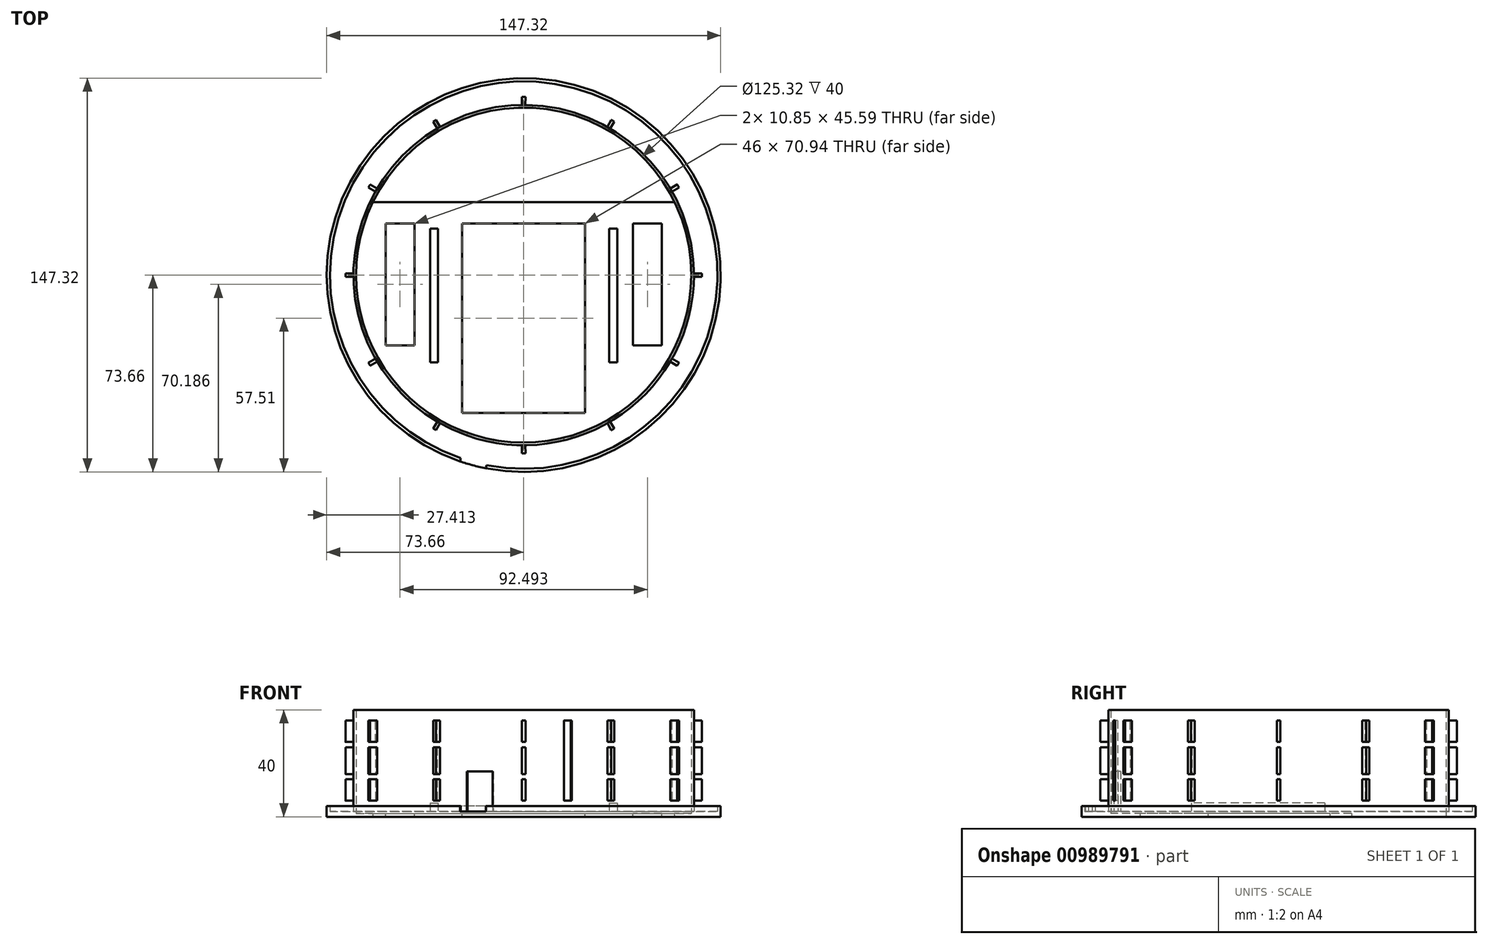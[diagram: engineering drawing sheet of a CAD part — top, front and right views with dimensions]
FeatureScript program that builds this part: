
annotation { "Feature Type Name" : "Feature", "Feature Type Description" : "" }
export const myFeature = defineFeature(function(context is Context, id is Id, definition is map)
    precondition{}
    {
        {
            var Q0;
            Q0=qCreatedBy(makeId("Top.planeOp"),FACE);
            var sketch = newSketch(context, id + "F0", { "sketchPlane" : qUnion([Q0])});
            skCircle(sketch, "E0", {"center": v(0, 0) * mm, "radius": 63.66 * mm, "construction": true});
            skCircle(sketch, "E1", {"center": v(0, 0) * mm, "radius": 73.66 * mm});
            skCircle(sketch, "E2", {"center": v(0, 0) * mm, "radius": 62.66 * mm});
            skPoint(sketch, "E3", {"position": v(0, -63.66) * mm});
            skSolve(sketch);
        }
        {
            var Q0;
            Q0=makeQuery(id+"F0.imprint","IMPRINT",FACE,{"disambiguationData":[TD([[makeQuery(id+"F0.imprint","IMPRINT",EDGE,{"derivedFrom":sQuery(id+"F0.wireOp",EDGE,"E1")}),1.0]])]});
            extrude(context, id + "F1", {"entities" : qUnion([Q0]), "depth" : 2 * mm, "offsetDistance" : 25 * mm});
        }
        {
            var Q0;
            Q0=makeQuery(id+"F1.opExtrude","CAP_FACE",FACE,{"disambiguationData":[OSD([sQuery(id+"F0.wireOp",EDGE,"E1"),sQuery(id+"F0.wireOp",EDGE,"E2")])],"isStart":false});
            var sketch = newSketch(context, id + "F2", { "sketchPlane" : qUnion([Q0])});
            skCircle(sketch, "E4.0", {"center": v(0, 0) * mm, "radius": 63.66 * mm});
            skCircle(sketch, "E5.0", {"center": v(0, 0) * mm, "radius": 62.66 * mm});
            skSolve(sketch);
        }
        {
            var Q0;
            Q0 = qSketchRegion(id + "F2", true);
            extrude(context, id + "F3", {"entities" : qUnion([Q0]), "operationType" : NewBodyOperationType.ADD, "depth" : 38 * mm, "offsetDistance" : 25 * mm});
        }
        {
            var Q0;
            Q0=makeQuery(id+"F1.opExtrude","CAP_FACE",FACE,{"disambiguationData":[OSD([sQuery(id+"F0.wireOp",EDGE,"E1"),sQuery(id+"F0.wireOp",EDGE,"E2")])],"isStart":false});
            var sketch = newSketch(context, id + "F4", { "sketchPlane" : qUnion([Q0])});
            skCircle(sketch, "E6.0", {"center": v(0, 0) * mm, "radius": 73.66 * mm});
            skCircle(sketch, "E7", {"center": v(0, 0) * mm, "radius": 72.46 * mm});
            skPoint(sketch, "E8", {"position": v(0, 72.46) * mm});
            skPoint(sketch, "E9", {"position": v(0, 73.66) * mm});
            skSolve(sketch);
        }
        {
            var Q0;
            Q0 = qSketchRegion(id + "F4", true);
            extrude(context, id + "F5", {"entities" : qUnion([Q0]), "operationType" : NewBodyOperationType.ADD, "depth" : 2 * mm, "offsetDistance" : 25 * mm});
        }
        {
            var Q0;
            Q0=qCreatedBy(makeId("Top.planeOp"),FACE);
            var sketch = newSketch(context, id + "F6", { "sketchPlane" : qUnion([Q0])});
            skLineSegment(sketch, "E10", {"start": v(0, 0) * mm, "end": v(0, -63.75) * mm, "construction": true});
            skSolve(sketch);
        }
        {
            var Q0;
            Q0=qCreatedBy(makeId("Front.planeOp"),FACE);
            var sketch = newSketch(context, id + "F7", { "sketchPlane" : qUnion([Q0])});
            skLineSegment(sketch, "E11", {"start": v(63.66, 40) * mm, "end": v(63.66, 2) * mm, "construction": true});
            skLineSegment(sketch, "E12", {"start": v(-63.66, 2) * mm, "end": v(-63.66, 40) * mm, "construction": true});
            skPoint(sketch, "E13", {"position": v(-63.66, 21) * mm});
            skLineSegment(sketch, "E14.bottom", {"start": v(-63.66, 26) * mm, "end": v(-66.66, 26) * mm});
            skLineSegment(sketch, "E14.top", {"start": v(-63.66, 16) * mm, "end": v(-66.66, 16) * mm});
            skLineSegment(sketch, "E14.left", {"start": v(-63.66, 26) * mm, "end": v(-63.66, 16) * mm});
            skLineSegment(sketch, "E14.right", {"start": v(-66.66, 26) * mm, "end": v(-66.66, 16) * mm});
            skLineSegment(sketch, "E15.bottom", {"start": v(-63.66, 28) * mm, "end": v(-66.66, 28) * mm});
            skLineSegment(sketch, "E15.top", {"start": v(-63.66, 36) * mm, "end": v(-66.66, 36) * mm});
            skLineSegment(sketch, "E15.left", {"start": v(-63.66, 28) * mm, "end": v(-63.66, 36) * mm});
            skLineSegment(sketch, "E15.right", {"start": v(-66.66, 28) * mm, "end": v(-66.66, 36) * mm});
            skLineSegment(sketch, "E16.bottom", {"start": v(-63.66, 14) * mm, "end": v(-66.66, 14) * mm});
            skLineSegment(sketch, "E16.top", {"start": v(-63.66, 6) * mm, "end": v(-66.66, 6) * mm});
            skLineSegment(sketch, "E16.left", {"start": v(-63.66, 14) * mm, "end": v(-63.66, 6) * mm});
            skLineSegment(sketch, "E16.right", {"start": v(-66.66, 14) * mm, "end": v(-66.66, 6) * mm});
            skSolve(sketch);
        }
        {
            var Q0;
            Q0=qCreatedBy(makeId("Front.planeOp"),FACE);
            var sketch = newSketch(context, id + "F8", { "sketchPlane" : qUnion([Q0])});
            skLineSegment(sketch, "E17", {"start": v(0, 0) * mm, "end": v(0, 90.7) * mm, "construction": true});
            skSolve(sketch);
        }
        {
            var Q0;
            Q0 = qSketchRegion(id + "F7", true);
            var Q1;
            Q1=sQuery(id+"F8.wireOp",EDGE,"E17");
            revolve(context, id + "F9", {"surfaceOperationType" : NewSurfaceOperationType.NEW, "entities" : qUnion([Q0]), "axis" : qUnion([Q1]), "revolveType" : RevolveType.SYMMETRIC, "angle" : 1.12 * degree});
        }
        {
            var Q0;
            Q0=makeQuery(id+"F9.opRevolve","SWEPT_BODY",BODY,{"disambiguationData":[OSD([sQuery(id+"F7.wireOp",EDGE,"E15.bottom"),sQuery(id+"F7.wireOp",EDGE,"E15.top"),sQuery(id+"F7.wireOp",EDGE,"E15.left"),sQuery(id+"F7.wireOp",EDGE,"E15.right")])]});
            var Q1;
            Q1=makeQuery(id+"F9.opRevolve","SWEPT_BODY",BODY,{"disambiguationData":[OSD([sQuery(id+"F7.wireOp",EDGE,"E14.bottom"),sQuery(id+"F7.wireOp",EDGE,"E14.top"),sQuery(id+"F7.wireOp",EDGE,"E14.left"),sQuery(id+"F7.wireOp",EDGE,"E14.right")])]});
            var Q2;
            Q2=makeQuery(id+"F9.opRevolve","SWEPT_BODY",BODY,{"disambiguationData":[OSD([sQuery(id+"F7.wireOp",EDGE,"E16.bottom"),sQuery(id+"F7.wireOp",EDGE,"E16.top"),sQuery(id+"F7.wireOp",EDGE,"E16.left"),sQuery(id+"F7.wireOp",EDGE,"E16.right")])]});
            var Q3;
            Q3=sQuery(id+"F8.wireOp",EDGE,"E17");
            circularPattern(context, id + "F10", {"entities" : qUnion([Q0, Q1, Q2]), "axis" : qUnion([Q3]), "angle" : 360 * degree, "instanceCount" : 12, "equalSpace" : true});
        }
        {
            var Q0;
            Q0=qCreatedBy(makeId("Top.planeOp"),FACE);
            var sketch = newSketch(context, id + "F11", { "sketchPlane" : qUnion([Q0])});
            skPoint(sketch, "E18.0", {"position": v(31.83, -55.13) * mm});
            skLineSegment(sketch, "E19", {"start": v(0, 0) * mm, "end": v(31.83, -55.13) * mm, "construction": true});
            skCircle(sketch, "E20.0", {"center": v(0, 0) * mm, "radius": 62.66 * mm, "construction": true});
            skPoint(sketch, "E21", {"position": v(0, -62.66) * mm});
            skPoint(sketch, "E22", {"position": v(31.33, -54.27) * mm});
            skLineSegment(sketch, "E23", {"start": v(0, -62.66) * mm, "end": v(31.33, -54.27) * mm, "construction": true});
            skPoint(sketch, "E24", {"position": v(15.67, -58.46) * mm});
            skLineSegment(sketch, "E25", {"start": v(15.67, -58.46) * mm, "end": v(0, 0) * mm, "construction": true});
            skLineSegment(sketch, "E26.MirrorCS", {"start": v(-15.67, -58.46) * mm, "end": v(0, 0) * mm, "construction": true});
            skCircle(sketch, "E27.0", {"center": v(0, 0) * mm, "radius": 63.66 * mm, "construction": true});
            skLineSegment(sketch, "E28", {"start": v(15.67, -58.46) * mm, "end": v(16.48, -61.5) * mm, "construction": true});
            skLineSegment(sketch, "E29", {"start": v(-15.67, -58.46) * mm, "end": v(-16.48, -61.5) * mm, "construction": true});
            skSolve(sketch);
        }
        {
            var Q0;
            Q0=sQuery(id+"F11.wireOp",VERTEX,"E28.end");
            var Q1;
            Q1=sQuery(id+"F11.wireOp",EDGE,"E25");
            cPlane(context, id + "F12", {"entities" : qUnion([Q0, Q1]), "cplaneType" : CPlaneType.LINE_POINT, "offset" : 25 * mm, "width" : 150 * mm, "height" : 150 * mm});
        }
        {
            var Q0;
            Q0=qCreatedBy(id+"F12.planeOp",FACE);
            var sketch = newSketch(context, id + "F13", { "sketchPlane" : qUnion([Q0])});
            skLineSegment(sketch, "E30.0", {"start": v(61.5, 2) * mm, "end": v(61.5, 40) * mm, "construction": true});
            skLineSegment(sketch, "E30.1", {"start": v(-61.5, 40) * mm, "end": v(-61.5, 2) * mm, "construction": true});
            skLineSegment(sketch, "E31", {"start": v(61.5, 40) * mm, "end": v(-61.5, 40) * mm, "construction": true});
            skLineSegment(sketch, "E32", {"start": v(61.5, 2) * mm, "end": v(-61.5, 2) * mm});
            skLineSegment(sketch, "E33.bottom", {"start": v(1.5, 36) * mm, "end": v(-1.5, 36) * mm});
            skLineSegment(sketch, "E33.top", {"start": v(1.5, 6) * mm, "end": v(-1.5, 6) * mm});
            skLineSegment(sketch, "E33.left", {"start": v(1.5, 36) * mm, "end": v(1.5, 6) * mm});
            skLineSegment(sketch, "E33.right", {"start": v(-1.5, 36) * mm, "end": v(-1.5, 6) * mm});
            skLineSegment(sketch, "E34", {"start": v(61.5, 21) * mm, "end": v(-61.5, 21) * mm, "construction": true});
            skPoint(sketch, "E35.0", {"position": v(61.5, 36) * mm});
            skPoint(sketch, "E35.1", {"position": v(61.5, 6) * mm});
            skLineSegment(sketch, "E36", {"start": v(61.5, 36) * mm, "end": v(-61.5, 36) * mm, "construction": true});
            skLineSegment(sketch, "E37", {"start": v(61.5, 6) * mm, "end": v(-61.5, 6) * mm, "construction": true});
            skSolve(sketch);
        }
        {
            var Q0;
            Q0 = qSketchRegion(id + "F13", true);
            extrude(context, id + "F14", {"entities" : qUnion([Q0]), "operationType" : NewBodyOperationType.REMOVE, "endBound" : BoundingType.UP_TO_NEXT, "depth" : 25 * mm, "offsetDistance" : 25 * mm});
        }
        {
            var Q0;
            Q0=sQuery(id+"F11.wireOp",VERTEX,"E29.end");
            var Q1;
            Q1=sQuery(id+"F11.wireOp",EDGE,"E26.MirrorCS");
            cPlane(context, id + "F15", {"entities" : qUnion([Q0, Q1]), "cplaneType" : CPlaneType.LINE_POINT, "offset" : 25 * mm, "width" : 150 * mm, "height" : 150 * mm});
        }
        {
            var Q0;
            Q0=qCreatedBy(id+"F15.planeOp",FACE);
            var sketch = newSketch(context, id + "F16", { "sketchPlane" : qUnion([Q0])});
            skLineSegment(sketch, "E38.0", {"start": v(61.5, 2) * mm, "end": v(61.5, 40) * mm, "construction": true});
            skLineSegment(sketch, "E38.1", {"start": v(-61.5, 40) * mm, "end": v(-61.5, 2) * mm, "construction": true});
            skLineSegment(sketch, "E39", {"start": v(61.5, 40) * mm, "end": v(-61.5, 40) * mm, "construction": true});
            skLineSegment(sketch, "E40", {"start": v(-61.5, 2) * mm, "end": v(61.5, 2) * mm, "construction": true});
            skLineSegment(sketch, "E41.bottom", {"start": v(-5, 17) * mm, "end": v(5, 17) * mm});
            skLineSegment(sketch, "E41.top", {"start": v(-5, 2) * mm, "end": v(5, 2) * mm});
            skLineSegment(sketch, "E41.left", {"start": v(-5, 17) * mm, "end": v(-5, 2) * mm});
            skLineSegment(sketch, "E41.right", {"start": v(5, 17) * mm, "end": v(5, 2) * mm});
            skSolve(sketch);
        }
        {
            var Q0;
            Q0 = qSketchRegion(id + "F16", true);
            extrude(context, id + "F17", {"entities" : qUnion([Q0]), "operationType" : NewBodyOperationType.REMOVE, "endBound" : BoundingType.SYMMETRIC, "depth" : 25 * mm, "offsetDistance" : 25 * mm});
        }
        {
            var Q0;
            Q0=qCreatedBy(makeId("Top.planeOp"),FACE);
            var sketch = newSketch(context, id + "F18", { "sketchPlane" : qUnion([Q0])});
            skCircle(sketch, "E42.0", {"center": v(0, 0) * mm, "radius": 62.66 * mm, "construction": true});
            skLineSegment(sketch, "E43", {"start": v(-56.38, 27.34) * mm, "end": v(56.38, 27.34) * mm});
            skPoint(sketch, "E44", {"position": v(0, 27.34) * mm});
            skPoint(sketch, "E45", {"position": v(0, -62.66) * mm});
            skArc(sketch, "E46", {"start": v(-56.38, 27.34) * mm, "mid": v(0, -62.66) * mm, "end": v(56.38, 27.34) * mm});
            skSolve(sketch);
        }
        {
            var Q0;
            Q0 = qSketchRegion(id + "F18", true);
            extrude(context, id + "F19", {"entities" : qUnion([Q0]), "operationType" : NewBodyOperationType.ADD, "depth" : 1.2 * mm, "offsetDistance" : 25 * mm});
        }
        {
            var Q0;
            Q0=makeQuery(id+"F19.opExtrude","CAP_FACE",FACE,{"disambiguationData":[OSD([sQuery(id+"F18.wireOp",EDGE,"E43"),sQuery(id+"F18.wireOp",EDGE,"E46")])],"isStart":false});
            var sketch = newSketch(context, id + "F20", { "sketchPlane" : qUnion([Q0])});
            skLineSegment(sketch, "E47.bottom", {"start": v(-35, 17.34) * mm, "end": v(-32, 17.34) * mm});
            skLineSegment(sketch, "E47.top", {"start": v(-35, -32.66) * mm, "end": v(-32, -32.66) * mm});
            skLineSegment(sketch, "E47.left", {"start": v(-35, 17.34) * mm, "end": v(-35, -32.66) * mm});
            skLineSegment(sketch, "E47.right", {"start": v(-32, 17.34) * mm, "end": v(-32, -32.66) * mm});
            skLineSegment(sketch, "E48.bottom", {"start": v(32, 17.34) * mm, "end": v(35, 17.34) * mm});
            skLineSegment(sketch, "E48.top", {"start": v(32, -32.66) * mm, "end": v(35, -32.66) * mm});
            skLineSegment(sketch, "E48.left", {"start": v(32, 17.34) * mm, "end": v(32, -32.66) * mm});
            skLineSegment(sketch, "E48.right", {"start": v(35, 17.34) * mm, "end": v(35, -32.66) * mm});
            skLineSegment(sketch, "E49", {"start": v(-32, 17.34) * mm, "end": v(32, 17.34) * mm, "construction": true});
            skPoint(sketch, "E50", {"position": v(0, 17.34) * mm});
            skSolve(sketch);
        }
        {
            var Q0;
            Q0 = qSketchRegion(id + "F20", true);
            extrude(context, id + "F21", {"entities" : qUnion([Q0]), "operationType" : NewBodyOperationType.ADD, "depth" : 4 * mm, "offsetDistance" : 25 * mm});
        }
        {
            var Q0;
            Q0=makeQuery(id+"F19.opExtrude","CAP_FACE",FACE,{"disambiguationData":[OSD([sQuery(id+"F18.wireOp",EDGE,"E43"),sQuery(id+"F18.wireOp",EDGE,"E46")])],"isStart":false});
            var sketch = newSketch(context, id + "F22", { "sketchPlane" : qUnion([Q0])});
            skLineSegment(sketch, "E51.bottom", {"start": v(-23, 19.32) * mm, "end": v(23, 19.32) * mm});
            skLineSegment(sketch, "E51.top", {"start": v(-23, -51.62) * mm, "end": v(23, -51.62) * mm});
            skLineSegment(sketch, "E51.left", {"start": v(-23, 19.32) * mm, "end": v(-23, -51.62) * mm});
            skLineSegment(sketch, "E51.right", {"start": v(23, 19.32) * mm, "end": v(23, -51.62) * mm});
            skLineSegment(sketch, "E52.bottom", {"start": v(-51.67, 19.32) * mm, "end": v(-40.82, 19.32) * mm});
            skLineSegment(sketch, "E52.top", {"start": v(-51.67, -26.27) * mm, "end": v(-40.82, -26.27) * mm});
            skLineSegment(sketch, "E52.left", {"start": v(-51.67, 19.32) * mm, "end": v(-51.67, -26.27) * mm});
            skLineSegment(sketch, "E52.right", {"start": v(-40.82, 19.32) * mm, "end": v(-40.82, -26.27) * mm});
            skLineSegment(sketch, "E53", {"start": v(-40.82, 19.32) * mm, "end": v(-23, 19.32) * mm, "construction": true});
            skLineSegment(sketch, "E54.MirrorCS", {"start": v(51.67, 19.32) * mm, "end": v(51.67, -26.27) * mm});
            skLineSegment(sketch, "E55.MirrorCS", {"start": v(40.82, 19.32) * mm, "end": v(40.82, -26.27) * mm});
            skLineSegment(sketch, "E56.MirrorCS", {"start": v(51.67, -26.27) * mm, "end": v(40.82, -26.27) * mm});
            skLineSegment(sketch, "E57.MirrorCS", {"start": v(51.67, 19.32) * mm, "end": v(40.82, 19.32) * mm});
            skSolve(sketch);
        }
        {
            var Q0;
            Q0 = qSketchRegion(id + "F22", true);
            extrude(context, id + "F23", {"entities" : qUnion([Q0]), "operationType" : NewBodyOperationType.REMOVE, "endBound" : BoundingType.UP_TO_NEXT, "oppositeDirection" : true, "depth" : 25 * mm, "offsetDistance" : 25 * mm});
        }
    });
